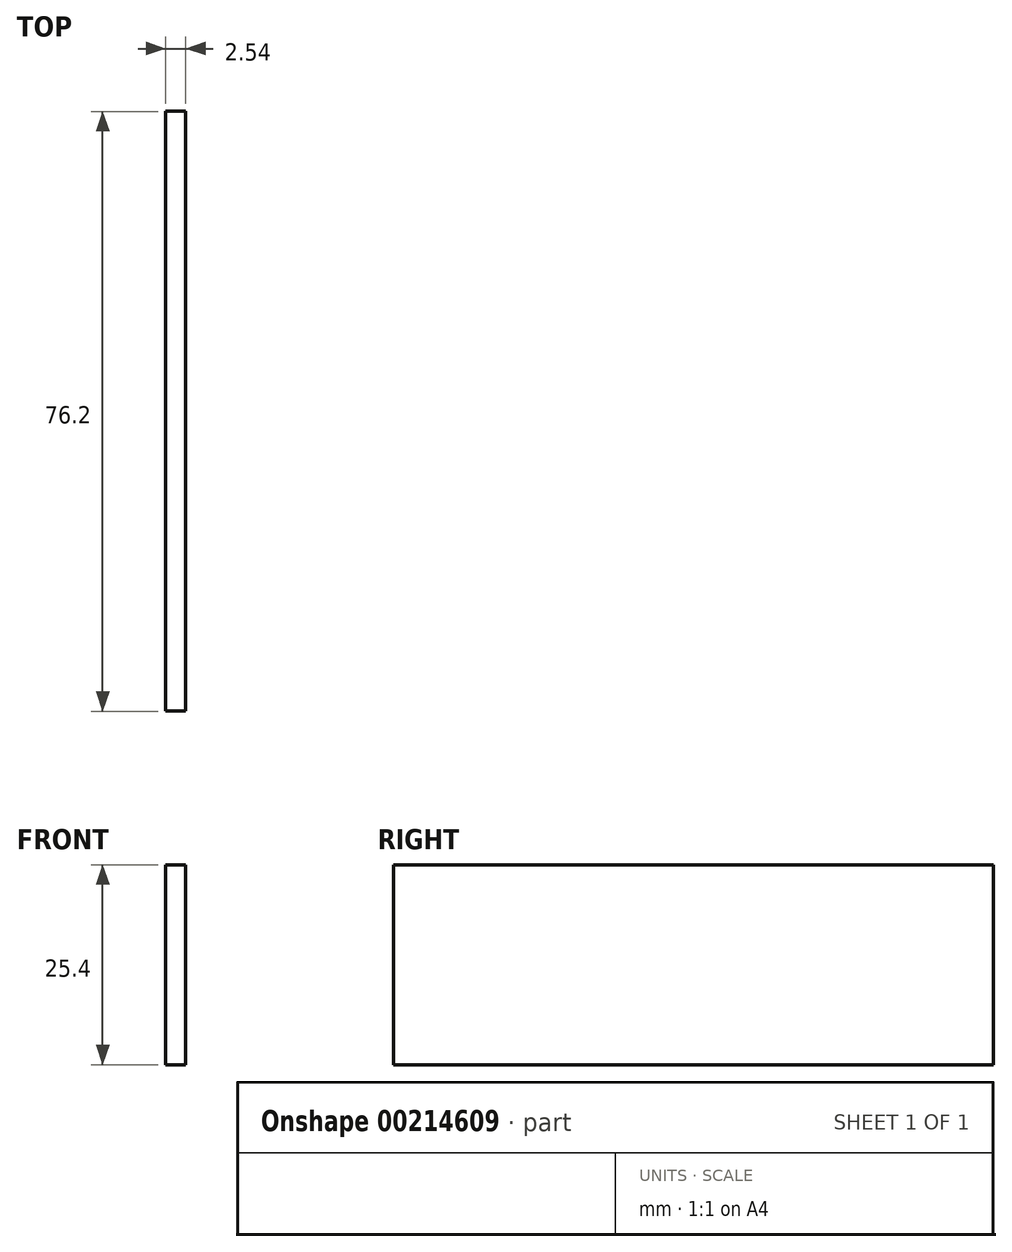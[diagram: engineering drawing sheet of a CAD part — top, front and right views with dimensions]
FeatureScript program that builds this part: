
annotation { "Feature Type Name" : "Feature", "Feature Type Description" : "" }
export const myFeature = defineFeature(function(context is Context, id is Id, definition is map)
    precondition{}
    {
        {
            var Q0;
            Q0=qCreatedBy(makeId("Right.planeOp"),FACE);
            var sketch = newSketch(context, id + "F0", { "sketchPlane" : qUnion([Q0])});
            skLineSegment(sketch, "E0.bottom", {"start": v(-27.22, 0.68) * mm, "end": v(48.98, 0.68) * mm});
            skLineSegment(sketch, "E0.top", {"start": v(-27.22, -24.72) * mm, "end": v(48.98, -24.72) * mm});
            skLineSegment(sketch, "E0.left", {"start": v(-27.22, 0.68) * mm, "end": v(-27.22, -24.72) * mm});
            skLineSegment(sketch, "E0.right", {"start": v(48.98, 0.68) * mm, "end": v(48.98, -24.72) * mm});
            skSolve(sketch);
        }
        {
            var Q0;
            Q0=makeQuery(id+"F0.imprint","IMPRINT",FACE,{"disambiguationData":[TD([[makeQuery(id+"F0.imprint","IMPRINT",EDGE,{"derivedFrom":sQuery(id+"F0.wireOp",EDGE,"E0.bottom")}),-1.0]])]});
            extrude(context, id + "F1", {"entities" : qUnion([Q0]), "depth" : 2.54 * mm});
        }
    });
